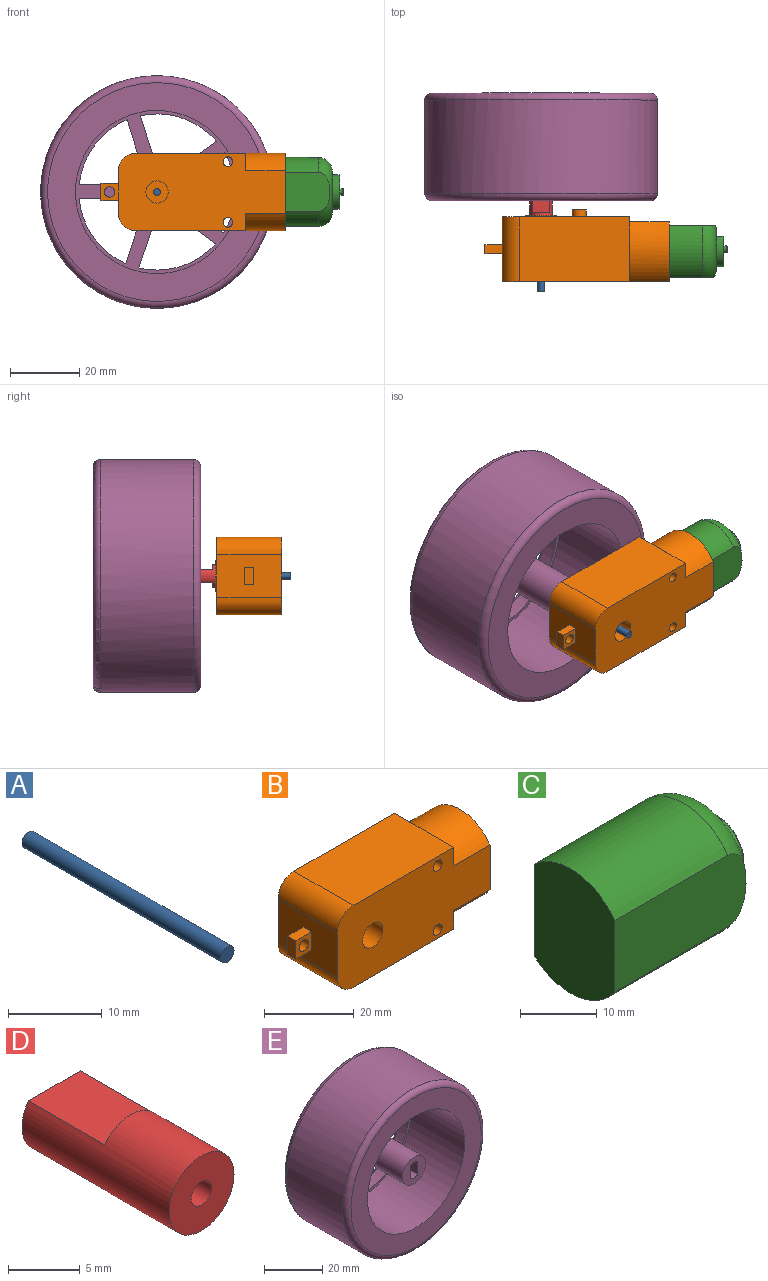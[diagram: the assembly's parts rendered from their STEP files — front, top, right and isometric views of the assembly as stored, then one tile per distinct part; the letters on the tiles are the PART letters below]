
ASSEMBLY  parts=5 mates=4
PART A: 3 faces, bbox 2x30x2 mm
  f0: cylinder r=1mm len=30mm, axis (0,1,0), area 188.5mm2, adj f1,f2
  f1: plane 2x2mm, normal (0,-1,0), area 3.1mm2, adj f0
  f2: plane 2x2mm, normal (0,1,0), area 3.1mm2, adj f0
PART B: 36 faces, bbox 53.1x20.7x22.3 mm
  f0: plane 36.7x22.3mm, normal (0,1,0), area 722mm2, adj f3,f5,f6,f7,f8,f9,f10,f12
  f1: cylinder r=3.2mm len=6.85mm, axis (0,1,0), area 137.7mm2, adj f33,f35
  f2: plane 9.35x5.08mm, normal (1,0,0), area 14mm2, adj f6,f13,f27
  f3: plane 22.3x9.35mm, normal (1,0,0), area 47.7mm2, adj f0,f6,f9,f25,f26,f27
  f4: plane 9.35x5.08mm, normal (1,0,0), area 14mm2, adj f9,f13,f25
  f5: plane 18.7x12.3mm, normal (-1,0,0), area 217mm2, adj f0,f7,f8,f13,f16,f17,f18,f19
  f6: plane 31.7x18.7mm, normal (0,0,1), area 592.8mm2, adj f0,f2,f3,f7,f13
  f7: cylinder r=5mm len=18.7mm, axis (0,1,0), area 146.9mm2, adj f0,f5,f6,f13
  f8: cylinder r=5mm len=18.7mm, axis (0,1,0), area 146.9mm2, adj f0,f5,f9,f13
  f9: plane 31.7x18.7mm, normal (0,0,-1), area 592.8mm2, adj f0,f3,f4,f8,f13
  f10: cylinder r=1.4mm len=18.7mm, axis (0,1,0), area 164.5mm2, adj f0,f13
  f11: cylinder r=3.2mm len=6.4mm, axis (0,1,0), area 127.7mm2, adj f13,f32
  f12: cylinder r=1.4mm len=18.7mm, axis (0,1,0), area 164.5mm2, adj f0,f13
  f13: plane 48.1x22.3mm, normal (0,-1,0), area 901.7mm2, adj f2,f4,f5,f6,f7,f8,f9,f10
  f14: cylinder r=2mm len=4mm, axis (0,-1,0), area 25.1mm2, adj f0,f15
  f15: plane 4x4mm, normal (0,1,0), area 12.6mm2, adj f14
  f16: plane 5x5mm, normal (0,-1,0), area 17.9mm2, adj f5,f17,f19,f20,f21
  f17: plane 5x2.6mm, normal (0,0,1), area 13mm2, adj f5,f16,f18,f20
  f18: plane 5x5mm, normal (0,1,0), area 17.9mm2, adj f5,f17,f19,f20,f21
  f19: plane 5x2.6mm, normal (0,0,-1), area 13mm2, adj f5,f16,f18,f20
  f20: plane 5x2.6mm, normal (-1,0,0), area 13mm2, adj f16,f17,f18,f19
  f21: cylinder r=1.5mm len=3mm, axis (0,-1,0), area 24.5mm2, adj f16,f18
  f22: cylinder r=9.95mm len=14.9mm, axis (-1,0,0), area 193.4mm2, adj f23,f28,f29,f30
  f23: plane 14.62x11.4mm, normal (0,-1,0), area 166.7mm2, adj f22,f24,f29,f30
  f24: cylinder r=9.95mm len=14.9mm, axis (-1,0,0), area 193.4mm2, adj f23,f28,f29,f30
  f25: cylinder r=11.15mm len=17.3mm, axis (-1,0,0), area 227.3mm2, adj f3,f4,f13,f26,f29
  f26: plane 15.64x11.4mm, normal (0,1,0), area 178.2mm2, adj f3,f25,f27,f29
  f27: cylinder r=11.15mm len=17.3mm, axis (-1,0,0), area 227.3mm2, adj f2,f3,f13,f26,f29
  f28: plane 11.42x11.4mm, normal (0,1,0), area 130.1mm2, adj f22,f24,f29,f30
  f29: plane 22.3x17.3mm, normal (1,0,0), area 76.6mm2, adj f13,f22,f23,f24,f25,f26,f27,f28
  f30: plane 19.9x14.9mm, normal (1,0,0), area 264.7mm2, adj f22,f23,f24,f28
  f31: cylinder r=1mm len=6mm, axis (0,1,0), area 37.7mm2, adj f32,f33
  f32: plane 6.4x6.4mm, normal (0,-1,0), area 29mm2, adj f11,f31
  f33: plane 6.4x6.4mm, normal (0,1,0), area 29mm2, adj f1,f31
  f34: cylinder r=4.4mm len=8.8mm, axis (0,-1,0), area 13.8mm2, adj f0,f35
  f35: plane 8.8x8.8mm, normal (0,1,0), area 28.7mm2, adj f1,f34
PART C: 14 faces, bbox 28.2x21.6x21.6 mm
  f0: plane 11.9x11.9mm, normal (1,0,0), area 38.3mm2, adj f6,f7,f8
  f1: plane 24.82x14.62mm, normal (0,1,0), area 353.1mm2, adj f2,f4,f5,f6
  f2: cylinder r=9.95mm len=20.9mm, axis (-1,0,0), area 354.6mm2, adj f1,f3,f5,f6
  f3: plane 24.24x11.42mm, normal (0,-1,0), area 269.2mm2, adj f2,f4,f5,f6
  f4: cylinder r=9.95mm len=20.9mm, axis (-1,0,0), area 354.6mm2, adj f1,f3,f5,f6
  f5: plane 19.9x14.9mm, normal (-1,0,0), area 264.7mm2, adj f1,f2,f3,f4
  f6: torus R=5.95mm, axis (-1,0,0), area 233.4mm2, adj f0,f1,f2,f3,f4
  f7: plane 6.7x2.29mm, normal (0,1,0), area 14.5mm2, adj f0,f8,f9,f13
  f8: cylinder r=5mm len=10mm, axis (-1,0,0), area 48.4mm2, adj f0,f7,f13
  f9: plane 9.6x8.55mm, normal (1,0,0), area 64.9mm2, adj f7,f10,f13
  f10: cylinder r=1mm len=2mm, axis (-1,0,0), area 5mm2, adj f9,f12
  f11: plane 1.6x1.6mm, normal (1,0,0), area 2mm2, adj f12
  f12: torus R=0.8mm, axis (1,0,0), area 1.8mm2, adj f10,f11
  f13: torus R=4.8mm, axis (1,0,0), area 7.6mm2, adj f7,f8,f9
PART D: 8 faces, bbox 6.4x14.5x6.4 mm
  f0: cylinder r=3.2mm len=14.5mm, axis (0,-1,0), area 202.5mm2, adj f2,f3,f4,f5,f6,f7
  f1: cylinder r=1mm len=14.5mm, axis (0,-1,0), area 91.1mm2, adj f2,f3
  f2: plane 6.4x3.84mm, normal (0,1,0), area 19.9mm2, adj f0,f1,f4,f6
  f3: plane 6.4x6.4mm, normal (0,-1,0), area 29mm2, adj f0,f1
  f4: plane 7.5x5.12mm, normal (0,0,-1), area 38.4mm2, adj f0,f2,f5
  f5: plane 5.12x1.28mm, normal (0,1,0), area 4.6mm2, adj f0,f4
  f6: plane 7.5x5.12mm, normal (0,0,1), area 38.4mm2, adj f0,f2,f7
  f7: plane 5.12x1.28mm, normal (0,1,0), area 4.6mm2, adj f0,f6
PART E: 53 faces, bbox 72.5x31x72.5 mm
  f0: plane 30x5.12mm, normal (-1,0,0), area 153.6mm2, adj f1,f3,f5,f27
  f1: cylinder r=3.2mm len=30mm, axis (0,1,0), area 123.6mm2, adj f0,f2,f5,f27
  f2: plane 30x5.12mm, normal (1,0,0), area 153.6mm2, adj f1,f3,f5,f27
  f3: cylinder r=3.2mm len=30mm, axis (0,1,0), area 123.6mm2, adj f0,f2,f5,f27
  f4: cylinder r=5.6mm len=25mm, axis (0,1,0), area 879.6mm2, adj f5,f28
  f5: plane 11.2x11.2mm, normal (0,-1,0), area 75.5mm2, adj f0,f1,f2,f3,f4
  f6: cylinder r=7.5mm len=4.26mm, axis (0,-1,0), area 21.5mm2, adj f7,f21,f28,f50
  f7: plane 15.18x4mm, normal (-1,0,0), area 60.7mm2, adj f6,f8,f28,f49
  f8: cylinder r=22.5mm len=18.7mm, axis (0,-1,0), area 97.1mm2, adj f7,f21,f28,f51
  f9: plane 12.28x8.92mm, normal (-0.81,0,0.59), area 60.7mm2, adj f10,f22,f28,f46
  f10: cylinder r=7.5mm len=5mm, axis (0,-1,0), area 21.5mm2, adj f9,f11,f28,f48
  f11: plane 14.44x4.69mm, normal (-0.31,0,-0.95), area 60.7mm2, adj f10,f22,f28,f47
  f12: plane 12.28x8.92mm, normal (-0.81,0,-0.59), area 60.7mm2, adj f13,f23,f28,f42
  f13: cylinder r=7.5mm len=5.26mm, axis (0,-1,0), area 21.5mm2, adj f12,f14,f28,f44
  f14: plane 12.28x8.92mm, normal (0.81,0,-0.59), area 60.7mm2, adj f13,f23,f28,f43
  f15: plane 14.44x4.69mm, normal (0.31,0,-0.95), area 60.7mm2, adj f16,f24,f28,f38
  f16: cylinder r=7.5mm len=5mm, axis (0,-1,0), area 21.5mm2, adj f15,f17,f28,f40
  f17: plane 12.28x8.92mm, normal (0.81,0,0.59), area 60.7mm2, adj f16,f24,f28,f39
  f18: plane 15.18x4mm, normal (1,0,0), area 60.7mm2, adj f19,f25,f28,f34
  f19: cylinder r=7.5mm len=4.26mm, axis (0,-1,0), area 21.5mm2, adj f18,f20,f28,f36
  f20: plane 14.44x4.69mm, normal (-0.31,0,0.95), area 60.7mm2, adj f19,f25,f28,f35
  f21: plane 14.44x4.69mm, normal (0.31,0,0.95), area 60.7mm2, adj f6,f8,f28,f52
  f22: cylinder r=22.5mm len=21.98mm, axis (0,-1,0), area 97.1mm2, adj f9,f11,f28,f45
  f23: cylinder r=22.5mm len=23.11mm, axis (0,-1,0), area 97.1mm2, adj f12,f14,f28,f41
  f24: cylinder r=22.5mm len=21.98mm, axis (0,-1,0), area 97.1mm2, adj f15,f17,f28,f37
  f25: cylinder r=22.5mm len=18.7mm, axis (0,-1,0), area 97.1mm2, adj f18,f20,f28,f33
  f26: cylinder r=33.5mm len=67mm, axis (0,-1,0), area 5683.1mm2, adj f31,f32
  f27: plane 63x63mm, normal (0,1,0), area 1662.2mm2, adj f0,f1,f2,f3,f32,f33,f34,f35
  f28: plane 47x47mm, normal (0,-1,0), area 523.9mm2, adj f4,f6,f7,f8,f9,f10,f11,f12
  f29: cylinder r=23.5mm len=47mm, axis (0,1,0), area 3839mm2, adj f28,f30
  f30: plane 63x63mm, normal (0,-1,0), area 1382.3mm2, adj f29,f31
  f31: torus R=31.5mm, axis (0,-1,0), area 646.9mm2, adj f26,f30
  f32: torus R=31.5mm, axis (0,1,0), area 646.9mm2, adj f26,f27
  f33: torus R=23.5mm, axis (0,1,0), area 40mm2, adj f25,f27,f34,f35
  f34: cylinder r=1mm len=17.06mm, axis (0,0,1), area 24.9mm2, adj f18,f27,f33,f36
  f35: cylinder r=1mm len=16.53mm, axis (-0.95,0,-0.31), area 24.9mm2, adj f20,f27,f33,f36
  f36: torus R=6.5mm, axis (0,1,0), area 8.9mm2, adj f19,f27,f34,f35
  f37: torus R=23.5mm, axis (0,1,0), area 40mm2, adj f24,f27,f38,f39
  f38: cylinder r=1mm len=16.53mm, axis (0.95,0,0.31), area 24.9mm2, adj f15,f27,f37,f40
  f39: cylinder r=1mm len=14.39mm, axis (-0.59,0,0.81), area 24.9mm2, adj f17,f27,f37,f40
  f40: torus R=6.5mm, axis (0,1,0), area 8.9mm2, adj f16,f27,f38,f39
  f41: torus R=23.5mm, axis (0,1,0), area 40mm2, adj f23,f27,f42,f43
  f42: cylinder r=1mm len=14.39mm, axis (0.59,0,-0.81), area 24.9mm2, adj f12,f27,f41,f44
  f43: cylinder r=1mm len=14.39mm, axis (0.59,0,0.81), area 24.9mm2, adj f14,f27,f41,f44
  f44: torus R=6.5mm, axis (0,1,0), area 8.9mm2, adj f13,f27,f42,f43
  f45: torus R=23.5mm, axis (0,1,0), area 40mm2, adj f22,f27,f46,f47
  f46: cylinder r=1mm len=14.39mm, axis (-0.59,0,-0.81), area 24.9mm2, adj f9,f27,f45,f48
  f47: cylinder r=1mm len=16.53mm, axis (0.95,0,-0.31), area 24.9mm2, adj f11,f27,f45,f48
  f48: torus R=6.5mm, axis (0,1,0), area 8.9mm2, adj f10,f27,f46,f47
  f49: cylinder r=1mm len=17.06mm, axis (0,0,-1), area 24.9mm2, adj f7,f27,f50,f51
  f50: torus R=6.5mm, axis (0,1,0), area 8.9mm2, adj f6,f27,f49,f52
  f51: torus R=23.5mm, axis (0,1,0), area 40mm2, adj f8,f27,f49,f52
  f52: cylinder r=1mm len=16.53mm, axis (-0.95,0,0.31), area 24.9mm2, adj f21,f27,f50,f51
PLACE A rot(axis=(0,1,0),0.6deg) t=(-21.85,12.87,-6.55)mm
PLACE B t=(-21.85,9.87,-6.48)mm fixed
PLACE C t=(-21.85,9.87,-6.48)mm
PLACE D rot(axis=(0,1,0),0.6deg) t=(-21.85,10.37,-6.55)mm
PLACE E rot(axis=(0,-1,0),89.4deg) t=(-29.05,49.87,-6.48)mm
MATE fastened A.f0 <-> E.f1  axis (0,1,0) through (-29.05,27.87,-6.48)mm
MATE fastened A.f0 <-> D.f0  axis (0,1,0) through (-29.05,27.87,-6.48)mm
MATE fastened B.f30 <-> C.f5  axis (1,0,0) through (-3.5,9.36,-6.48)mm
MATE revolute A.f0 <-> B.f1  axis (0,1,0) through (-29.05,12.87,-6.48)mm
